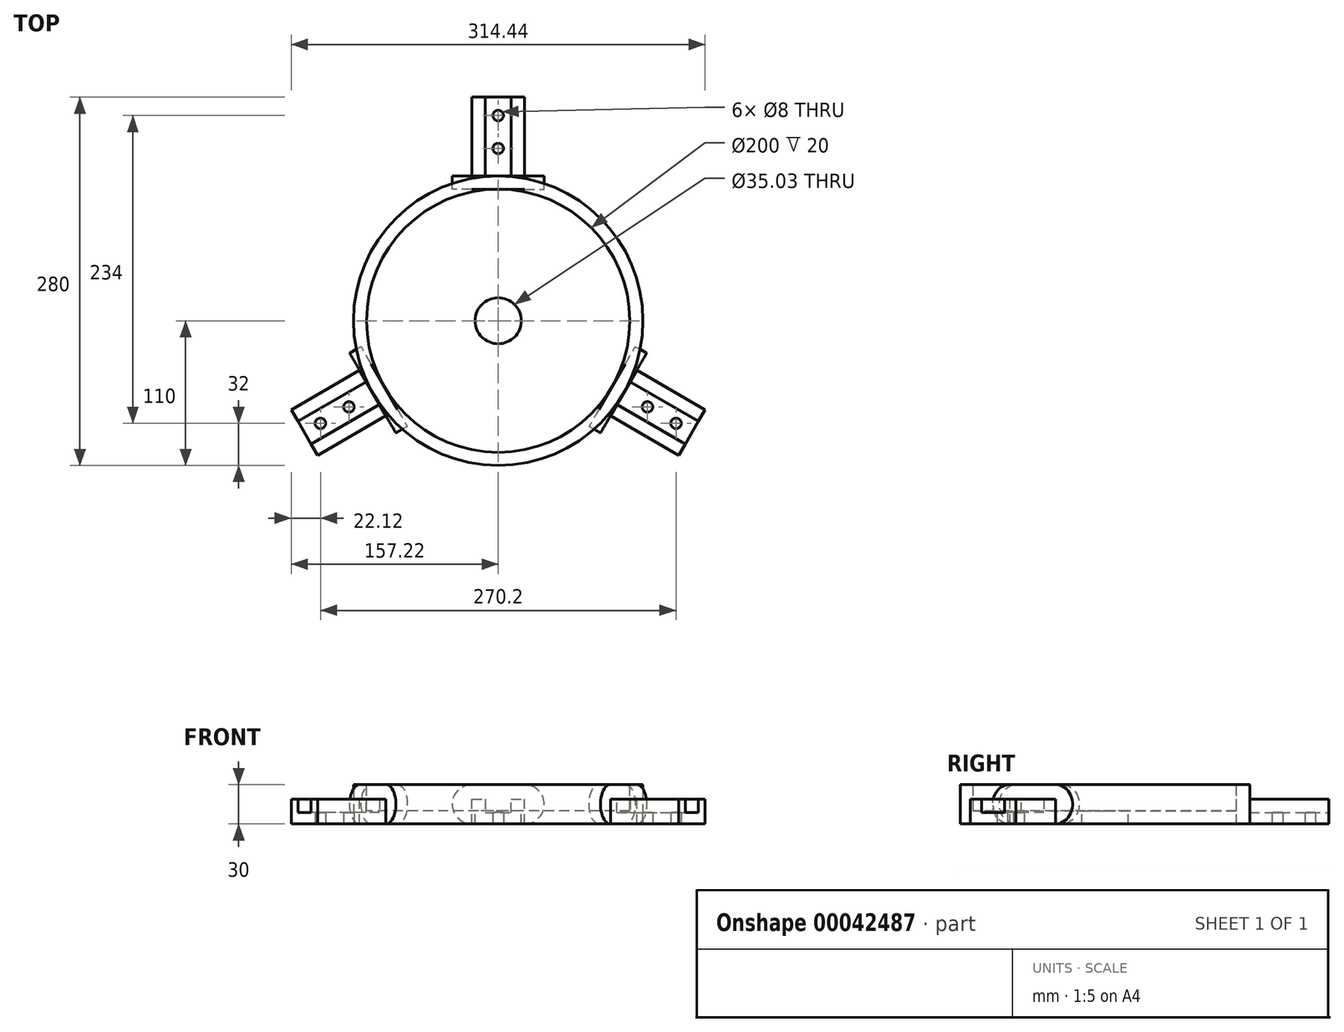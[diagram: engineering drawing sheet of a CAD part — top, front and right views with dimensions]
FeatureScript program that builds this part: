
annotation { "Feature Type Name" : "Feature", "Feature Type Description" : "" }
export const myFeature = defineFeature(function(context is Context, id is Id, definition is map)
    precondition{}
    {
        {
            var Q0;
            Q0=qCreatedBy(makeId("Front.planeOp"),FACE);
            var sketch = newSketch(context, id + "F0", { "sketchPlane" : qUnion([Q0])});
            skLineSegment(sketch, "E0.bottom", {"start": v(-20, 0) * mm, "end": v(20, 0) * mm});
            skLineSegment(sketch, "E0.top", {"start": v(-20, 18.73) * mm, "end": v(-10, 18.73) * mm});
            skLineSegment(sketch, "E0.left", {"start": v(-20, 0) * mm, "end": v(-20, 18.73) * mm});
            skLineSegment(sketch, "E0.right", {"start": v(20, 0) * mm, "end": v(20, 18.73) * mm});
            skLineSegment(sketch, "E1", {"start": v(-10, 18.73) * mm, "end": v(-10, 8.73) * mm});
            skLineSegment(sketch, "E2", {"start": v(-10, 8.73) * mm, "end": v(10, 8.73) * mm});
            skLineSegment(sketch, "E3", {"start": v(10, 8.73) * mm, "end": v(10, 18.73) * mm});
            skLineSegment(sketch, "E4.trimOffspring", {"start": v(10, 18.73) * mm, "end": v(20, 18.73) * mm});
            skSolve(sketch);
        }
        {
            var Q0;
            Q0=qSketchRegion(id+"F0",true);
            extrude(context, id + "F1", {"entities" : qUnion([Q0]), "depth" : 60 * mm});
        }
        {
            var Q0;
            Q0=makeQuery(id+"F1.opExtrude","CAP_FACE",FACE,{"disambiguationData":[OSD([sQuery(id+"F0.wireOp",EDGE,"E0.bottom"),sQuery(id+"F0.wireOp",EDGE,"E0.top"),sQuery(id+"F0.wireOp",EDGE,"E0.left"),sQuery(id+"F0.wireOp",EDGE,"E0.right"),sQuery(id+"F0.wireOp",EDGE,"E1"),sQuery(id+"F0.wireOp",EDGE,"E2"),sQuery(id+"F0.wireOp",EDGE,"E3"),sQuery(id+"F0.wireOp",EDGE,"E4.trimOffspring")])],"isStart":false});
            var sketch = newSketch(context, id + "F2", { "sketchPlane" : qUnion([Q0])});
            skLineSegment(sketch, "E5.bottom", {"start": v(-9.65, 92.48) * mm, "end": v(9.65, 92.48) * mm});
            skPoint(sketch, "E6.visualSharp", {"position": v(-41.42, 92.48) * mm});
            skPoint(sketch, "E7.visualSharp", {"position": v(41.42, 92.48) * mm});
            skLineSegment(sketch, "E8", {"start": v(-20, 0) * mm, "end": v(20, 0) * mm});
            skLineSegment(sketch, "E9", {"start": v(-20, 30) * mm, "end": v(20, 30) * mm});
            skLineSegment(sketch, "E10", {"start": v(0, 0) * mm, "end": v(0, 47.83) * mm, "construction": true});
            skArc(sketch, "E11", {"start": v(-20, 0) * mm, "mid": v(-35, 15) * mm, "end": v(-20, 30) * mm});
            skArc(sketch, "E12", {"start": v(20, 0) * mm, "mid": v(35, 15) * mm, "end": v(20, 30) * mm});
            skSolve(sketch);
        }
        {
            var Q0;
            Q0=qSketchRegion(id+"F2",true);
            extrude(context, id + "F3", {"entities" : qUnion([Q0]), "operationType" : NewBodyOperationType.ADD, "depth" : 5 * mm});
        }
        {
            var Q0;
            Q0=qCreatedBy(makeId("Top.planeOp"),FACE);
            var sketch = newSketch(context, id + "F4", { "sketchPlane" : qUnion([Q0])});
            skCircle(sketch, "E13", {"center": v(0, -39) * mm, "radius": 4 * mm});
            skCircle(sketch, "E14", {"center": v(0, -14) * mm, "radius": 4 * mm});
            skSolve(sketch);
        }
        {
            var Q0;
            Q0=qSketchRegion(id+"F4",true);
            extrude(context, id + "F5", {"entities" : qUnion([Q0]), "operationType" : NewBodyOperationType.REMOVE, "endBound" : BoundingType.THROUGH_ALL, "depth" : 25 * mm});
        }
        {
            var Q0;
            Q0 = qSketchRegion(id + "F2", true);
            extrude(context, id + "F6", {"entities" : qUnion([Q0]), "operationType" : NewBodyOperationType.ADD, "depth" : 10 * mm});
        }
        {
            var Q0;
            Q0=makeQuery(id+"F6.opExtrude","CAP_FACE",FACE,{"disambiguationData":[OSD([sQuery(id+"F2.wireOp",EDGE,"E8"),sQuery(id+"F2.wireOp",EDGE,"E9"),sQuery(id+"F2.wireOp",EDGE,"E11"),sQuery(id+"F2.wireOp",EDGE,"E12")])],"isStart":false});
            cPlane(context, id + "F7", {"entities" : qUnion([Q0]), "cplaneType" : CPlaneType.OFFSET, "offset" : 100 * mm, "width" : 150 * mm, "height" : 150 * mm});
        }
        {
            var Q0;
            Q0=qCreatedBy(id+"F7.planeOp",FACE);
            var sketch = newSketch(context, id + "F8", { "sketchPlane" : qUnion([Q0])});
            skLineSegment(sketch, "E15", {"start": v(0, 0) * mm, "end": v(0, 30) * mm});
            skLineSegment(sketch, "E16", {"start": v(0, 0) * mm, "end": v(110, 0) * mm});
            skLineSegment(sketch, "E17", {"start": v(0, 30) * mm, "end": v(110, 30) * mm});
            skLineSegment(sketch, "E18", {"start": v(110, 30) * mm, "end": v(110, 0) * mm});
            skLineSegment(sketch, "E19", {"start": v(0, 0) * mm, "end": v(0, 80.64) * mm, "construction": true});
            skSolve(sketch);
        }
        {
            var Q0;
            Q0=qCreatedBy(id+"F7.planeOp",FACE);
            var sketch = newSketch(context, id + "F9", { "sketchPlane" : qUnion([Q0])});
            skLineSegment(sketch, "E20", {"start": v(0, -61.44) * mm, "end": v(0, 70.32) * mm, "construction": true});
            skSolve(sketch);
        }
        {
            var Q0;
            Q0=makeQuery(id+"F1.opExtrude","SWEPT_BODY",BODY,{"disambiguationData":[OSD([sQuery(id+"F0.wireOp",EDGE,"E0.bottom"),sQuery(id+"F0.wireOp",EDGE,"E0.top"),sQuery(id+"F0.wireOp",EDGE,"E0.left"),sQuery(id+"F0.wireOp",EDGE,"E0.right"),sQuery(id+"F0.wireOp",EDGE,"E1"),sQuery(id+"F0.wireOp",EDGE,"E2"),sQuery(id+"F0.wireOp",EDGE,"E3"),sQuery(id+"F0.wireOp",EDGE,"E4.trimOffspring")])]});
            var Q1;
            Q1=sQuery(id+"F8.wireOp",EDGE,"E15");
            circularPattern(context, id + "F10", {"entities" : qUnion([Q0]), "axis" : qUnion([Q1]), "angle" : 120 * degree, "instanceCount" : 3});
        }
        {
            var Q0;
            Q0 = qSketchRegion(id + "F8", true);
            var Q1;
            Q1=sQuery(id+"F9.wireOp",EDGE,"E20");
            revolve(context, id + "F11", {"entities" : qUnion([Q0]), "axis" : qUnion([Q1]), "revolveType" : RevolveType.FULL});
        }
        {
            var Q0;
            Q0=makeQuery(id+"F11.opRevolve","SWEPT_FACE",FACE,{"disambiguationData":[OSD([sQuery(id+"F8.wireOp",EDGE,"E17")])]});
            var sketch = newSketch(context, id + "F12", { "sketchPlane" : qUnion([Q0])});
            skCircle(sketch, "E21", {"center": v(0, -170) * mm, "radius": 100 * mm});
            skSolve(sketch);
        }
        {
            var Q0;
            Q0=makeQuery(id+"F12.imprint","IMPRINT",FACE,{"disambiguationData":[TD([[makeQuery(id+"F12.imprint","IMPRINT",EDGE,{"derivedFrom":sQuery(id+"F12.wireOp",EDGE,"E21")}),1.0]])]});
            extrude(context, id + "F13", {"entities" : qUnion([Q0]), "operationType" : NewBodyOperationType.REMOVE, "oppositeDirection" : true, "depth" : 20 * mm});
        }
        {
            var Q0;
            Q0=makeQuery(id+"F13.boolean.opBoolean","COPY",FACE,{"derivedFrom":makeQuery(id+"F13.opExtrude","CAP_FACE",FACE,{"disambiguationData":[OSD([sQuery(id+"F12.wireOp",EDGE,"E21")])],"isStart":false})});
            var sketch = newSketch(context, id + "F14", { "sketchPlane" : qUnion([Q0])});
            skCircle(sketch, "E22", {"center": v(0, -170) * mm, "radius": 17.52 * mm});
            skSolve(sketch);
        }
        {
            var Q0;
            Q0 = qSketchRegion(id + "F14", true);
            extrude(context, id + "F15", {"entities" : qUnion([Q0]), "operationType" : NewBodyOperationType.REMOVE, "endBound" : BoundingType.THROUGH_ALL, "oppositeDirection" : true, "depth" : 25 * mm});
        }
    });
